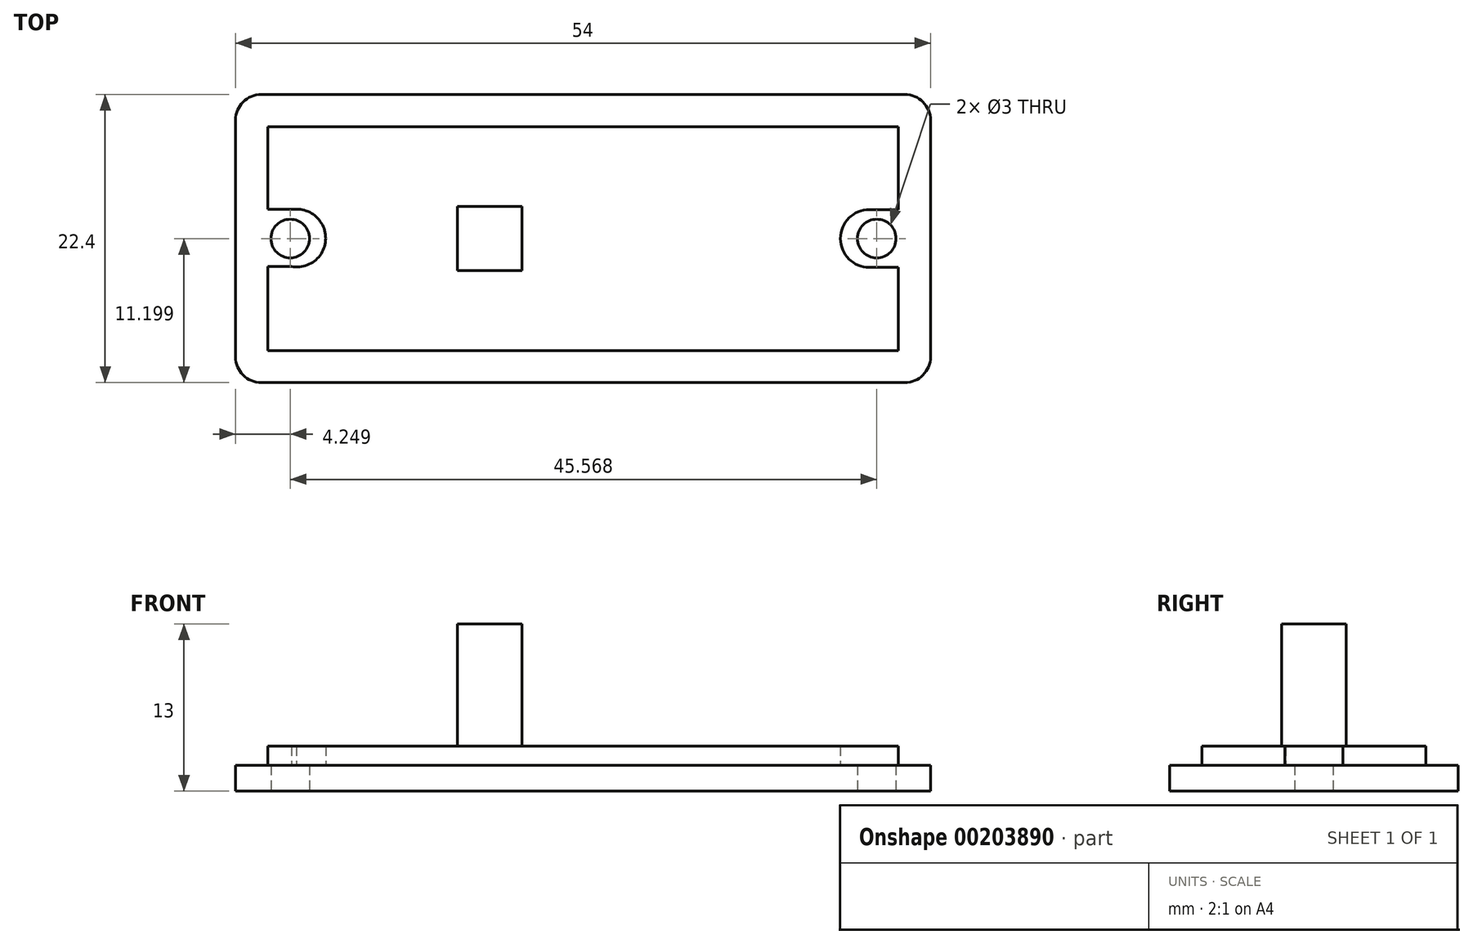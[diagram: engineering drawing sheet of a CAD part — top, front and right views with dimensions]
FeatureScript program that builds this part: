
annotation { "Feature Type Name" : "Feature", "Feature Type Description" : "" }
export const myFeature = defineFeature(function(context is Context, id is Id, definition is map)
    precondition{}
    {
        {
            var Q0;
            Q0=qCreatedBy(makeId("Top.planeOp"),FACE);
            var sketch = newSketch(context, id + "F0", { "sketchPlane" : qUnion([Q0])});
            skLineSegment(sketch, "E0.bottom", {"start": v(-25.61, 12.03) * mm, "end": v(28.39, 12.03) * mm});
            skLineSegment(sketch, "E0.top", {"start": v(-25.61, -10.37) * mm, "end": v(28.39, -10.37) * mm});
            skLineSegment(sketch, "E0.left", {"start": v(-25.61, 12.03) * mm, "end": v(-25.61, -10.37) * mm});
            skLineSegment(sketch, "E0.right", {"start": v(28.39, 12.03) * mm, "end": v(28.39, -10.37) * mm});
            skLineSegment(sketch, "E1.bottom", {"start": v(-23.11, 9.53) * mm, "end": v(25.89, 9.53) * mm});
            skLineSegment(sketch, "E1.top", {"start": v(-23.11, -7.87) * mm, "end": v(25.89, -7.87) * mm});
            skLineSegment(sketch, "E1.left", {"start": v(-23.11, 9.53) * mm, "end": v(-23.11, -7.87) * mm});
            skLineSegment(sketch, "E1.right", {"start": v(25.89, 9.53) * mm, "end": v(25.89, -7.87) * mm});
            skCircle(sketch, "E2", {"center": v(23.64, 0.83) * mm, "radius": 2.25 * mm});
            skLineSegment(sketch, "E3.bottom", {"start": v(23.64, 3.08) * mm, "end": v(25.89, 3.08) * mm});
            skLineSegment(sketch, "E3.top", {"start": v(23.64, -1.42) * mm, "end": v(25.89, -1.42) * mm});
            skLineSegment(sketch, "E3.left", {"start": v(23.64, 3.08) * mm, "end": v(23.64, -1.42) * mm});
            skLineSegment(sketch, "E3.right", {"start": v(25.89, 3.08) * mm, "end": v(25.89, -1.42) * mm});
            skCircle(sketch, "E4", {"center": v(-21.36, 0.83) * mm, "radius": 1.5 * mm});
            skCircle(sketch, "E5", {"center": v(24.2, 0.83) * mm, "radius": 1.5 * mm});
            skLineSegment(sketch, "E6.bottom", {"start": v(-8.37, 3.33) * mm, "end": v(-3.37, 3.33) * mm});
            skLineSegment(sketch, "E6.top", {"start": v(-8.37, -1.67) * mm, "end": v(-3.37, -1.67) * mm});
            skLineSegment(sketch, "E6.left", {"start": v(-8.37, 3.33) * mm, "end": v(-8.37, -1.67) * mm});
            skLineSegment(sketch, "E6.right", {"start": v(-3.37, 3.33) * mm, "end": v(-3.37, -1.67) * mm});
            skCircle(sketch, "E7", {"center": v(-20.86, 0.86) * mm, "radius": 2.25 * mm});
            skLineSegment(sketch, "E8.bottom", {"start": v(-20.9, 3.1) * mm, "end": v(-23.11, 3.1) * mm});
            skLineSegment(sketch, "E8.top", {"start": v(-20.9, -1.36) * mm, "end": v(-23.11, -1.36) * mm});
            skLineSegment(sketch, "E8.left", {"start": v(-20.9, 3.1) * mm, "end": v(-20.9, -1.36) * mm});
            skLineSegment(sketch, "E8.right", {"start": v(-23.11, 3.1) * mm, "end": v(-23.11, -1.36) * mm});
            skSolve(sketch);
        }
        {
            var Q0;
            {var subQ3=sQuery(id+"F0.wireOp",EDGE,"E1.top");Q0=makeQuery(id+"F0.imprint","IMPRINT",FACE,{"disambiguationData":[TD([[makeQuery(id+"F0.imprint","IMPRINT",EDGE,{"derivedFrom":subQ3}),1.0]])]});}
            var Q1;
            Q1=makeQuery(id+"F0.imprint","IMPRINT",FACE,{"disambiguationData":[TD([[makeQuery(id+"F0.imprint","IMPRINT",EDGE,{"derivedFrom":sQuery(id+"F0.wireOp",EDGE,"E6.bottom")}),-1.0]])]});
            var Q2;
            {var subQ0=sQuery(id+"F0.wireOp",EDGE,"E3.top");Q2=makeQuery(id+"F0.imprint","IMPRINT",FACE,{"disambiguationData":[TD([[makeQuery(id+"F0.imprint","IMPRINT",EDGE,{"derivedFrom":subQ0}),1.0]])]});}
            var Q3;
            {var subQ0=sQuery(id+"F0.wireOp",EDGE,"E3.left");var subQ3=sQuery(id+"F0.wireOp",EDGE,"E5");var subQ4=makeQuery(id+"F0.imprint","INTERSECT",VERTEX,{"disambiguationData":[OD(0.0)],"derivedFrom":[subQ0,subQ3]});Q3=makeQuery(id+"F0.imprint","IMPRINT",FACE,{"disambiguationData":[TD([[makeQuery(id+"F0.imprint","IMPRINT",EDGE,{"disambiguationData":[TD([[subQ4,1.0]])],"derivedFrom":subQ3}),-1.0]])]});}
            var Q4;
            {var subQ0=sQuery(id+"F0.wireOp",EDGE,"E3.bottom");Q4=makeQuery(id+"F0.imprint","IMPRINT",FACE,{"disambiguationData":[TD([[makeQuery(id+"F0.imprint","IMPRINT",EDGE,{"derivedFrom":subQ0}),-1.0]])]});}
            var Q5;
            {var subQ0=sQuery(id+"F0.wireOp",EDGE,"E3.left");var subQ4=sQuery(id+"F0.wireOp",EDGE,"E5");var subQ6=makeQuery(id+"F0.imprint","INTERSECT",VERTEX,{"disambiguationData":[OD(0.0)],"derivedFrom":[subQ0,subQ4]});Q5=makeQuery(id+"F0.imprint","IMPRINT",FACE,{"disambiguationData":[TD([[makeQuery(id+"F0.imprint","IMPRINT",EDGE,{"disambiguationData":[TD([[subQ6,-1.0]])],"derivedFrom":subQ4}),-1.0]])]});}
            var Q6;
            {var subQ0=sQuery(id+"F0.wireOp",EDGE,"e8dd041a-e369-4de5-9f56-f7fbeddcef8c.bottom");Q6=makeQuery(id+"F0.imprint","IMPRINT",FACE,{"disambiguationData":[TD([[makeQuery(id+"F0.imprint","IMPRINT",EDGE,{"derivedFrom":subQ0}),-1.0]])]});}
            var Q7;
            {var subQ0=sQuery(id+"F0.wireOp",EDGE,"e8dd041a-e369-4de5-9f56-f7fbeddcef8c.left");var subQ3=sQuery(id+"F0.wireOp",EDGE,"E4");var subQ6=makeQuery(id+"F0.imprint","INTERSECT",VERTEX,{"disambiguationData":[OD(0.0)],"derivedFrom":[subQ0,subQ3]});Q7=makeQuery(id+"F0.imprint","IMPRINT",FACE,{"disambiguationData":[TD([[makeQuery(id+"F0.imprint","IMPRINT",EDGE,{"disambiguationData":[TD([[subQ6,1.0]])],"derivedFrom":subQ3}),-1.0]])]});}
            var Q8;
            {var subQ0=sQuery(id+"F0.wireOp",EDGE,"e8dd041a-e369-4de5-9f56-f7fbeddcef8c.top");Q8=makeQuery(id+"F0.imprint","IMPRINT",FACE,{"disambiguationData":[TD([[makeQuery(id+"F0.imprint","IMPRINT",EDGE,{"derivedFrom":subQ0}),1.0]])]});}
            var Q9;
            {var subQ0=sQuery(id+"F0.wireOp",EDGE,"e8dd041a-e369-4de5-9f56-f7fbeddcef8c.left");var subQ4=sQuery(id+"F0.wireOp",EDGE,"E4");var subQ5=makeQuery(id+"F0.imprint","INTERSECT",VERTEX,{"disambiguationData":[OD(0.0)],"derivedFrom":[subQ0,subQ4]});Q9=makeQuery(id+"F0.imprint","IMPRINT",FACE,{"disambiguationData":[TD([[makeQuery(id+"F0.imprint","IMPRINT",EDGE,{"disambiguationData":[TD([[subQ5,-1.0]])],"derivedFrom":subQ4}),-1.0]])]});}
            var Q10;
            {var subQ0=sQuery(id+"F0.wireOp",EDGE,"E8.bottom");Q10=makeQuery(id+"F0.imprint","IMPRINT",FACE,{"disambiguationData":[TD([[makeQuery(id+"F0.imprint","IMPRINT",EDGE,{"derivedFrom":subQ0}),1.0]])]});}
            var Q11;
            {var subQ0=sQuery(id+"F0.wireOp",EDGE,"E8.right");var subQ1=sQuery(id+"F0.wireOp",EDGE,"E7");var subQ2=makeQuery(id+"F0.imprint","INTERSECT",VERTEX,{"derivedFrom":[subQ1,subQ0]});Q11=makeQuery(id+"F0.imprint","IMPRINT",FACE,{"disambiguationData":[TD([[makeQuery(id+"F0.imprint","IMPRINT",EDGE,{"disambiguationData":[TD([[subQ2,-1.0]])],"derivedFrom":subQ1}),-1.0]])]});}
            var Q12;
            Q12=makeQuery(id+"F0.imprint","IMPRINT",FACE,{"disambiguationData":[TD([[makeQuery(id+"F0.imprint","IMPRINT",EDGE,{"derivedFrom":sQuery(id+"F0.wireOp",EDGE,"E0.bottom")}),-1.0]])]});
            extrude(context, id + "F1", {"entities" : qUnion([Q0, Q1, Q2, Q3, Q4, Q5, Q6, Q7, Q8, Q9, Q10, Q11, Q12]), "depth" : 2 * mm});
        }
        {
            var Q0;
            Q0=makeQuery(id+"F0.imprint","IMPRINT",FACE,{"disambiguationData":[TD([[makeQuery(id+"F0.imprint","IMPRINT",EDGE,{"derivedFrom":sQuery(id+"F0.wireOp",EDGE,"E6.bottom")}),-1.0]])]});
            extrude(context, id + "F2", {"entities" : qUnion([Q0]), "operationType" : NewBodyOperationType.ADD, "depth" : 13 * mm});
        }
        {
            var Q0;
            {var subQ7=sQuery(id+"F0.wireOp",EDGE,"E1.bottom");Q0=makeQuery(id+"F0.imprint","IMPRINT",FACE,{"disambiguationData":[TD([[makeQuery(id+"F0.imprint","IMPRINT",EDGE,{"derivedFrom":subQ7}),-1.0]])]});}
            var Q1;
            Q1=makeQuery(id+"F0.imprint","IMPRINT",FACE,{"disambiguationData":[TD([[makeQuery(id+"F0.imprint","IMPRINT",EDGE,{"derivedFrom":sQuery(id+"F0.wireOp",EDGE,"E6.bottom")}),-1.0]])]});
            extrude(context, id + "F3", {"entities" : qUnion([Q0, Q1]), "operationType" : NewBodyOperationType.ADD, "depth" : 3.5 * mm});
        }
        {
            var Q0;
            Q0=makeQuery(id+"F1.opExtrude","SWEPT_EDGE",EDGE,{"disambiguationData":[OSD([sQuery(id+"F0.wireOp",EDGE,"E0.bottom"),sQuery(id+"F0.wireOp",EDGE,"E0.left")])]});
            var Q1;
            Q1=makeQuery(id+"F1.opExtrude","SWEPT_EDGE",EDGE,{"disambiguationData":[OSD([sQuery(id+"F0.wireOp",EDGE,"E0.top"),sQuery(id+"F0.wireOp",EDGE,"E0.left")])]});
            var Q2;
            Q2=makeQuery(id+"F1.opExtrude","SWEPT_EDGE",EDGE,{"disambiguationData":[OSD([sQuery(id+"F0.wireOp",EDGE,"E0.bottom"),sQuery(id+"F0.wireOp",EDGE,"E0.right")])]});
            var Q3;
            Q3=makeQuery(id+"F1.opExtrude","SWEPT_EDGE",EDGE,{"disambiguationData":[OSD([sQuery(id+"F0.wireOp",EDGE,"E0.top"),sQuery(id+"F0.wireOp",EDGE,"E0.right")])]});
            fillet(context, id + "F4", {"entities" : qUnion([Q0, Q1, Q2, Q3]), "radius" : 2 * mm, "tangentPropagation" : true, "allowEdgeOverflow" : false});
        }
    });
